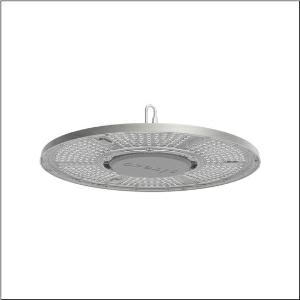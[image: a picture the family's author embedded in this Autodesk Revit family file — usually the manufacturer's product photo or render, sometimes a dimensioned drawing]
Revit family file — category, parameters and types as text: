
# Revit family: highbay_31-l_51hc42da4jmb
name_source: partatom
category: Lighting Fixtures
units: mm (PartAtom-declared; Revit-internal decimal feet)

## family parameters
Cut with Voids When Loaded = No
Host = Face
Light Source = No
Part Type = Normal
Room Calculation Point = No
Round Connector Dimension = Use Diameter
Shared = No

## types (1)
- Highbay 31-L (1 x LED, 20000 lm, 134 W, 4000K)
    Apparent Load = 134 VA
    CIE Flux Codes = 77 99 100 100 100
    Color Rendering = 80
    Color Temperature = 4000K
    Default Elevation = 1800 mm
    Description = Highbay 31-L, LED high bay luminaire, primary light control with lens, of PC, primary optical cover: cover panel, of PC, transparent, light emission: direct distribution, primary light characteristic: rotationally symmetric, installation type: suspended mounting, surface-mounted, LED, rated luminous flux: 20.000lm, luminous efficacy: 150lm/W, light colour: 840, colour temperature: 4000K, control gear: ECG DALI, with cable, 5x 1.0mm², free wire ends, mains connection: 220..240V, AC/DC, 0/50..60Hz, cable length: 1,5m, rated input power: 134W, housing, rotationally symmetric, of diecast aluminium, powder-coated, grey aluminium (RAL 9007), with hook on luminaire side, incl. screw, diameter: 404mm, protection rating (complete): IP65, insulation class (complete): insulation class I (protective earthing), certification: CE, ENEC, UKCA, protection symbol: D, impact resistance: IK08, permissible operating ambient temperature: -30..+45°C, standard: EN 60598-2-22, EN 60598, corresponds to IFS (International Featured Standards) requirements for safety and quality in the food industry, packaging unit: 1 piece
    Height = 141 mm
    Lamp = 1 x LED
    Lamp Light Flux = 20000 lm
    Lamp Power = 134 W
    Lamp count = 1
    Length = 406 mm
    Luminous efficacy = 149 lm/W
    Manufacturer = Siteco
    ModVariant = No
    Model = 51HC42DA4JMB
    Mounting Place = Ceiling
    Mounting Type = Pendant
    Number of Poles = 1
    OnlyDefault = Yes
    Power Factor = 1
    Product Name = Highbay 31-L
    Product group = LED high bay luminaire
    ProductGroupID = 903
    Protection Class = Protection class I
    Protection Degree = IP 65
    RLX_Detail_Level = 1
    RLX_Emergency_Light_Flux = 0 lm
    RLX_Emergency_Type = 0
    RLX_Emergency_Type_DB = No
    RlxData = <blob elided: 173205 chars, md5=41817fdf>
    Socket = socket
    Standby Power = 0 W
    System Light Flux = 20000 lm
    System Power = 134 W
    Type Comments = Product without accessories
    Type Image = l_1003610.jpg
    URL = http://relux.com
    VarID = ---
    Voltage = 0 V
    Weight = 0.00 kg
    Width = 0 mm  [stored 0 ft]

note: [stored X ft] marks values corroborated as IEEE doubles in the binary element streams (Revit-internal decimal feet)

## geometry (parser evidence)
native form markers: Blend x4, Sweep x10
no freeform markers — native parametric forms only
